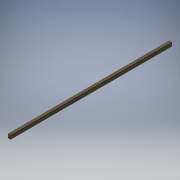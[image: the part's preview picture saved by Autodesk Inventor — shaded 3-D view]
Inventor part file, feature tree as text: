
AUTODESK INVENTOR PART (.ipt)
format: ipt  version: 2017 (Build 210142000, 142)  size: 98,816 bytes
history: native  units: mm
features: extrude x1, sketch x1
ambient origin geometry x8: Origin, YZ Plane, XZ Plane, XY Plane, X Axis, Y Axis, Z Axis, Center Point
bodies: Volumenkörper1 (feature_tree)
feature tree (2):
  extrude  "Extrusion1"  Depth=100.0mm
  sketch  "Skizze2"  dims[d2=60.0mm d3=100.0mm d4=4000.0mm d5=0.0mm]
